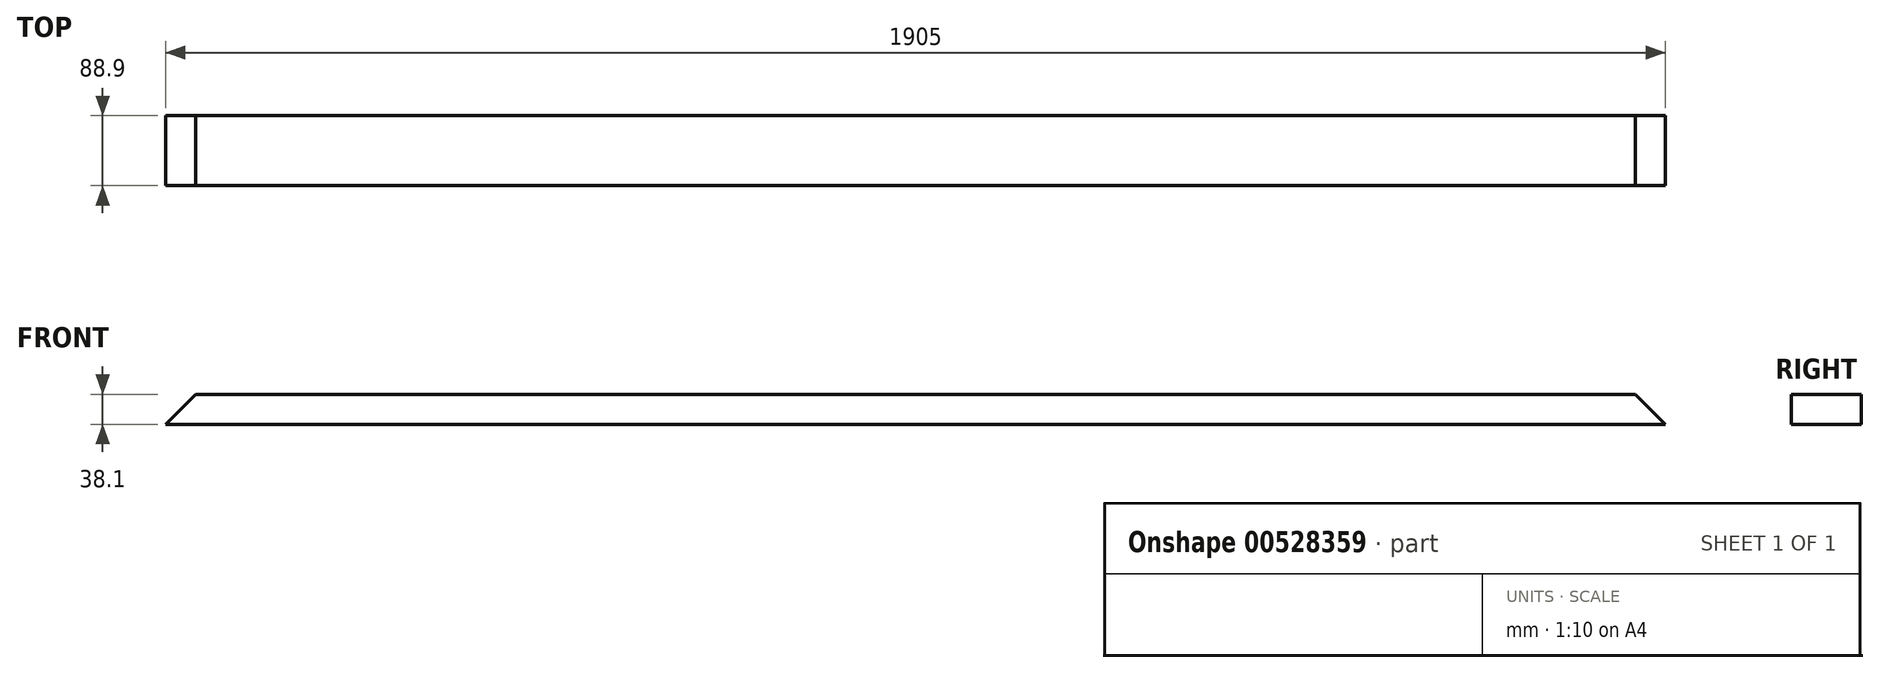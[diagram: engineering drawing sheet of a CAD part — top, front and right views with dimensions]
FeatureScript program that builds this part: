
annotation { "Feature Type Name" : "Feature", "Feature Type Description" : "" }
export const myFeature = defineFeature(function(context is Context, id is Id, definition is map)
    precondition{}
    {
        {
            var Q0;
            Q0=qCreatedBy(makeId("Front.planeOp"),FACE);
            var sketch = newSketch(context, id + "F0", { "sketchPlane" : qUnion([Q0])});
            skLineSegment(sketch, "E0", {"start": v(0, 0) * mm, "end": v(38.1, 38.1) * mm});
            skLineSegment(sketch, "E1", {"start": v(38.1, 38.1) * mm, "end": v(1866.9, 38.1) * mm});
            skLineSegment(sketch, "E2", {"start": v(1866.9, 38.1) * mm, "end": v(1905, 0) * mm});
            skLineSegment(sketch, "E3", {"start": v(1905, 0) * mm, "end": v(0, 0) * mm});
            skSolve(sketch);
        }
        {
            var Q0;
            Q0 = qSketchRegion(id + "F0", true);
            extrude(context, id + "F1", {"entities" : qUnion([Q0]), "depth" : 88.9 * mm, "offsetDistance" : 25.4 * mm});
        }
    });
